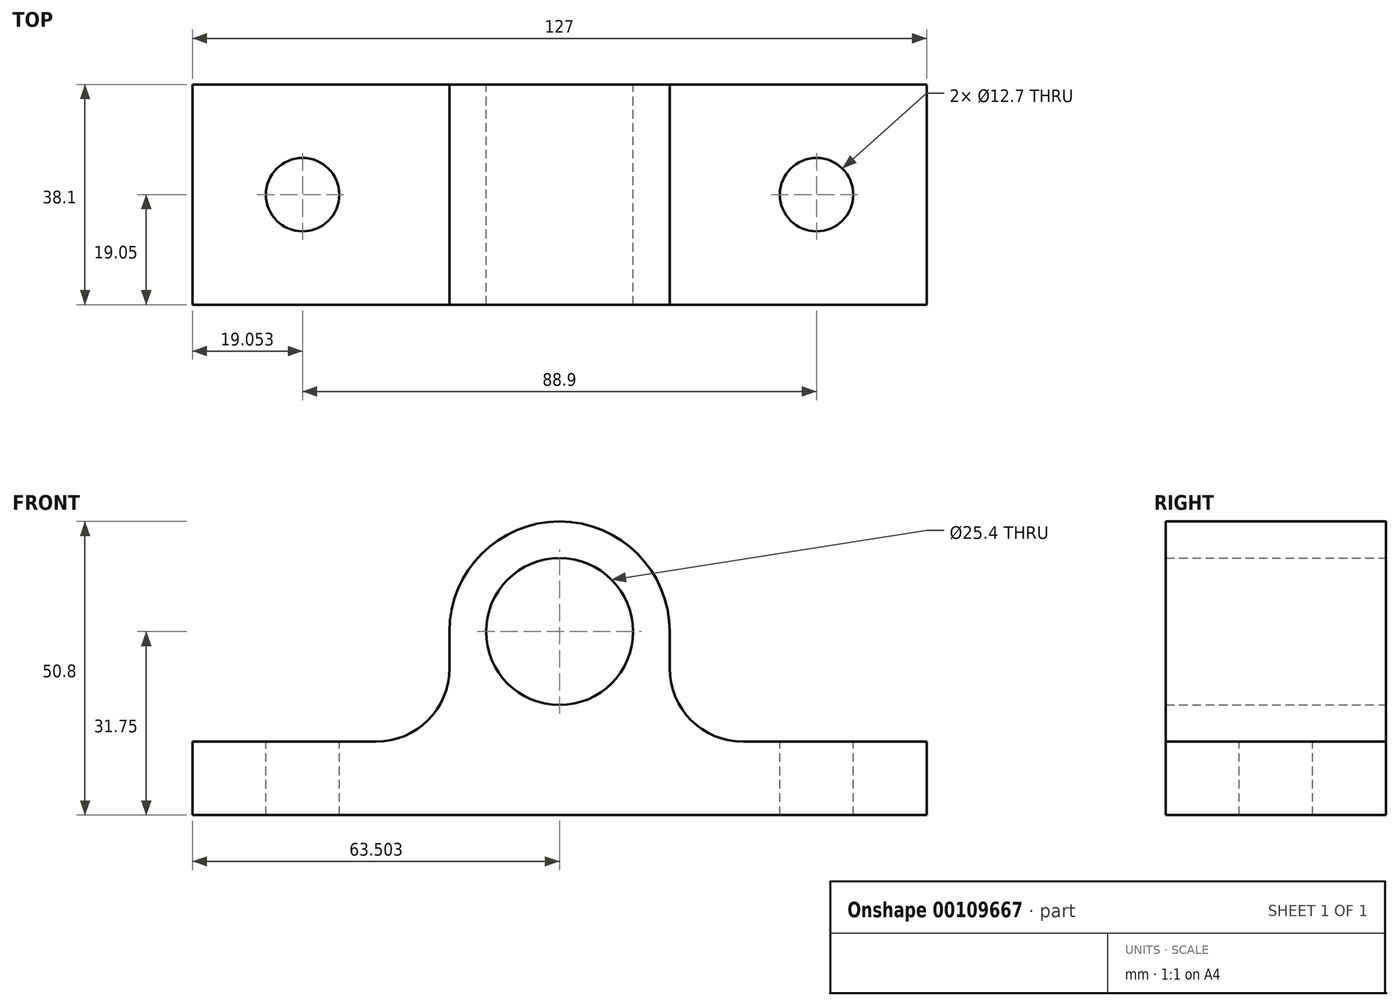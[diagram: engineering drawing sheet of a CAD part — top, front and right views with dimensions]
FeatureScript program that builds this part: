
annotation { "Feature Type Name" : "Feature", "Feature Type Description" : "" }
export const myFeature = defineFeature(function(context is Context, id is Id, definition is map)
    precondition{}
    {
        {
            var Q0;
            Q0=qCreatedBy(makeId("Front.planeOp"),FACE);
            var sketch = newSketch(context, id + "F0", { "sketchPlane" : qUnion([Q0])});
            skLineSegment(sketch, "E0", {"start": v(-53.84, 0) * mm, "end": v(73.16, 0) * mm});
            skLineSegment(sketch, "E1", {"start": v(73.16, 0) * mm, "end": v(73.16, 12.7) * mm});
            skLineSegment(sketch, "E2", {"start": v(-22.09, 12.7) * mm, "end": v(-53.84, 12.7) * mm});
            skLineSegment(sketch, "E3", {"start": v(-53.84, 12.7) * mm, "end": v(-53.84, 0) * mm});
            skCircle(sketch, "E4", {"center": v(9.66, 31.75) * mm, "radius": 19.05 * mm});
            skLineSegment(sketch, "E5", {"start": v(9.66, 31.75) * mm, "end": v(28.71, 31.75) * mm, "construction": true});
            skLineSegment(sketch, "E6", {"start": v(28.71, 31.75) * mm, "end": v(-9.39, 31.75) * mm, "construction": true});
            skLineSegment(sketch, "E7", {"start": v(-9.39, 31.75) * mm, "end": v(-9.39, 25.4) * mm});
            skLineSegment(sketch, "E8", {"start": v(28.71, 31.75) * mm, "end": v(28.71, 25.4) * mm});
            skPoint(sketch, "E9.newPointA", {"position": v(73.16, 12.7) * mm});
            skArc(sketch, "E9.filletArc", {"start": v(-22.09, 12.7) * mm, "mid": v(-13.1, 16.42) * mm, "end": v(-9.39, 25.4) * mm});
            skLineSegment(sketch, "E10", {"start": v(41.41, 12.7) * mm, "end": v(73.16, 12.7) * mm});
            skArc(sketch, "E11.filletArc", {"start": v(28.71, 25.4) * mm, "mid": v(32.43, 16.42) * mm, "end": v(41.41, 12.7) * mm});
            skCircle(sketch, "E12", {"center": v(9.66, 31.75) * mm, "radius": 12.7 * mm});
            skSolve(sketch);
        }
        {
            var Q0;
            Q0=makeQuery(id+"F0.imprint","IMPRINT",FACE,{"disambiguationData":[TD([[makeQuery(id+"F0.imprint","IMPRINT",EDGE,{"derivedFrom":sQuery(id+"F0.wireOp",EDGE,"E12")}),-1.0]])]});
            var Q1;
            Q1=makeQuery(id+"F0.imprint","IMPRINT",FACE,{"disambiguationData":[TD([[makeQuery(id+"F0.imprint","IMPRINT",EDGE,{"derivedFrom":sQuery(id+"F0.wireOp",EDGE,"E0")}),1.0]])]});
            extrude(context, id + "F1", {"entities" : qUnion([Q0, Q1]), "depth" : 38.1 * mm});
        }
        {
            var Q0;
            Q0=makeQuery(id+"F1.opExtrude","SWEPT_FACE",FACE,{"disambiguationData":[OSD([sQuery(id+"F0.wireOp",EDGE,"E2")])]});
            var sketch = newSketch(context, id + "F2", { "sketchPlane" : qUnion([Q0])});
            skCircle(sketch, "E13", {"center": v(-34.79, -19.05) * mm, "radius": 6.35 * mm});
            skCircle(sketch, "E14", {"center": v(54.11, -19.05) * mm, "radius": 6.35 * mm});
            skSolve(sketch);
        }
        {
            var Q0;
            Q0=makeQuery(id+"F2.imprint","IMPRINT",FACE,{"disambiguationData":[TD([[makeQuery(id+"F2.imprint","IMPRINT",EDGE,{"derivedFrom":sQuery(id+"F2.wireOp",EDGE,"E14")}),1.0]])]});
            var Q1;
            Q1=makeQuery(id+"F2.imprint","IMPRINT",FACE,{"disambiguationData":[TD([[makeQuery(id+"F2.imprint","IMPRINT",EDGE,{"derivedFrom":sQuery(id+"F2.wireOp",EDGE,"E13")}),1.0]])]});
            extrude(context, id + "F3", {"entities" : qUnion([Q0, Q1]), "operationType" : NewBodyOperationType.REMOVE, "oppositeDirection" : true, "depth" : 25.4 * mm});
        }
    });
